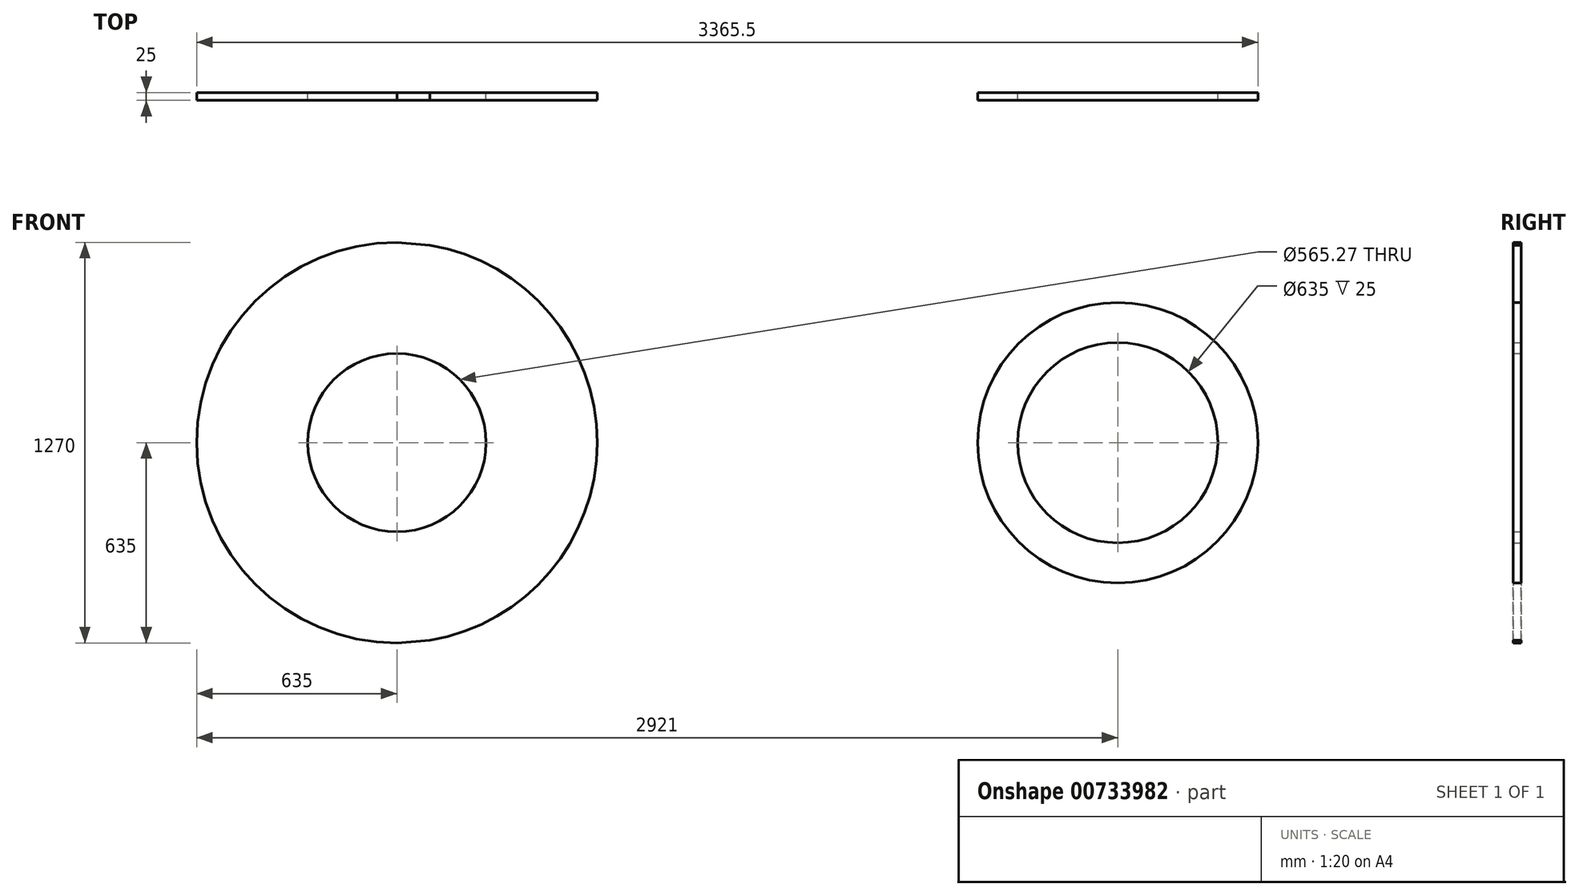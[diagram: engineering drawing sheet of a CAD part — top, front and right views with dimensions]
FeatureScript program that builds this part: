
annotation { "Feature Type Name" : "Feature", "Feature Type Description" : "" }
export const myFeature = defineFeature(function(context is Context, id is Id, definition is map)
    precondition{}
    {
        {
            var Q0;
            Q0=qCreatedBy(makeId("Front.planeOp"),FACE);
            var sketch = newSketch(context, id + "F0", { "sketchPlane" : qUnion([Q0])});
            skCircle(sketch, "E0", {"center": v(0, 0) * mm, "radius": 635 * mm});
            skCircle(sketch, "E1", {"center": v(2286, 0) * mm, "radius": 444.5 * mm});
            skLineSegment(sketch, "E2", {"start": v(0, 635) * mm, "end": v(2322.62, 442.99) * mm});
            skLineSegment(sketch, "E3", {"start": v(0, -635) * mm, "end": v(2322.62, -442.99) * mm});
            skCircle(sketch, "E4", {"center": v(2286, 0) * mm, "radius": 317.5 * mm});
            skCircle(sketch, "E5", {"center": v(0, 0) * mm, "radius": 282.63 * mm});
            skSolve(sketch);
        }
        {
            var Q0;
            Q0=makeQuery(id+"F0.imprint","IMPRINT",FACE,{"disambiguationData":[TD([[makeQuery(id+"F0.imprint","IMPRINT",EDGE,{"derivedFrom":sQuery(id+"F0.wireOp",EDGE,"E5")}),-1.0]])]});
            var Q1;
            {var subQ0=sQuery(id+"F0.wireOp",EDGE,"E2");var subQ1=sQuery(id+"F0.wireOp",EDGE,"E0");var subQ2=makeQuery(id+"F0.imprint","INTERSECT",VERTEX,{"disambiguationData":[OD(1.0)],"derivedFrom":[subQ1,subQ0]});Q1=makeQuery(id+"F0.imprint","IMPRINT",FACE,{"disambiguationData":[TD([[makeQuery(id+"F0.imprint","IMPRINT",EDGE,{"disambiguationData":[TD([[subQ2,1.0]])],"derivedFrom":subQ1}),-1.0]])]});}
            var Q2;
            Q2=makeQuery(id+"F0.imprint","IMPRINT",FACE,{"disambiguationData":[TD([[makeQuery(id+"F0.imprint","IMPRINT",EDGE,{"derivedFrom":sQuery(id+"F0.wireOp",EDGE,"E4")}),-1.0]])]});
            extrude(context, id + "F1", {"entities" : qUnion([Q0, Q1, Q2]), "depth" : 25 * mm, "offsetDistance" : 25.4 * mm});
        }
    });
